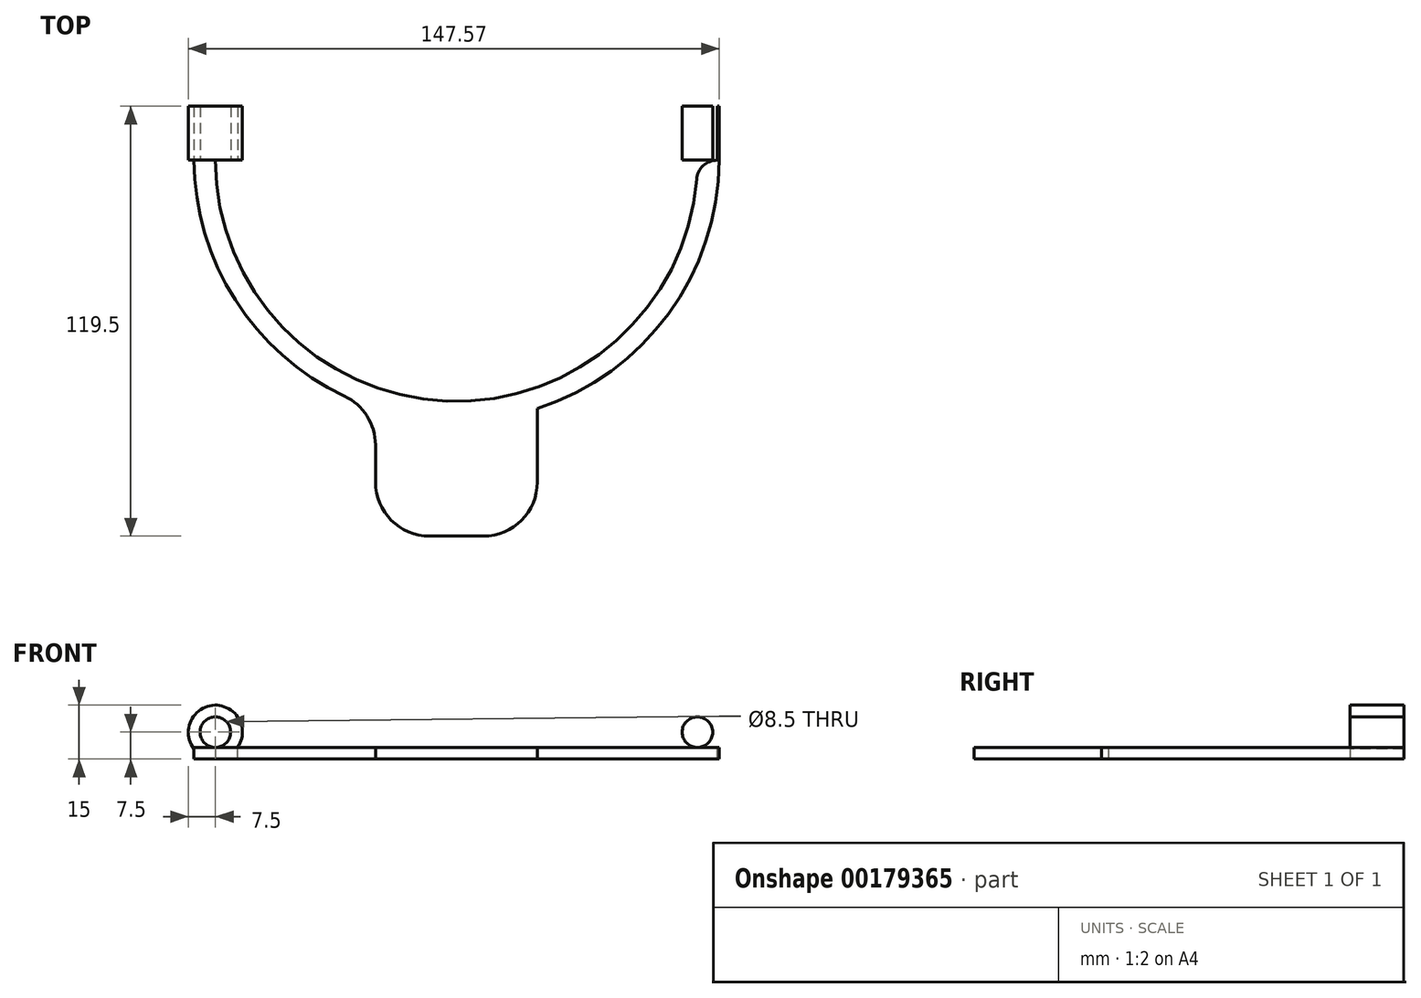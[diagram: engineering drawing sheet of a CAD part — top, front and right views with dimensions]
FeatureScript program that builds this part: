
annotation { "Feature Type Name" : "Feature", "Feature Type Description" : "" }
export const myFeature = defineFeature(function(context is Context, id is Id, definition is map)
    precondition{}
    {
        {
            var Q0;
            Q0=qCreatedBy(makeId("Front.planeOp"),FACE);
            var sketch = newSketch(context, id + "F0", { "sketchPlane" : qUnion([Q0])});
            skLineSegment(sketch, "E0.bottom", {"start": v(67, -4.25) * mm, "end": v(-67, -4.25) * mm, "construction": true});
            skLineSegment(sketch, "E0.top", {"start": v(67, 4.25) * mm, "end": v(-67, 4.25) * mm, "construction": true});
            skLineSegment(sketch, "E0.left", {"start": v(67, -4.25) * mm, "end": v(67, 4.25) * mm, "construction": true});
            skLineSegment(sketch, "E0.right", {"start": v(-67, -4.25) * mm, "end": v(-67, 4.25) * mm, "construction": true});
            skPoint(sketch, "E0.middle", {"position": v(0, 0) * mm});
            skArc(sketch, "E1", {"start": v(67, 4.25) * mm, "mid": v(71.25, 0) * mm, "end": v(67, -4.25) * mm});
            skArc(sketch, "E2", {"start": v(-67, 4.25) * mm, "mid": v(-71.25, 0) * mm, "end": v(-67, -4.25) * mm});
            skArc(sketch, "E3", {"start": v(-67, 4.25) * mm, "mid": v(-62.75, 0) * mm, "end": v(-67, -4.25) * mm});
            skArc(sketch, "E4", {"start": v(67, 4.25) * mm, "mid": v(62.75, 0) * mm, "end": v(67, -4.25) * mm});
            skCircle(sketch, "E5", {"center": v(-67, 0) * mm, "radius": 7.5 * mm});
            skCircle(sketch, "E6", {"center": v(67, 0) * mm, "radius": 7.5 * mm});
            skLineSegment(sketch, "E7.bottom", {"start": v(-67, -4.25) * mm, "end": v(67, -4.25) * mm});
            skLineSegment(sketch, "E7.top", {"start": v(-67, -7.5) * mm, "end": v(67, -7.5) * mm});
            skLineSegment(sketch, "E7.left", {"start": v(-67, -4.25) * mm, "end": v(-67, -7.5) * mm});
            skLineSegment(sketch, "E7.right", {"start": v(67, -4.25) * mm, "end": v(67, -7.5) * mm});
            skSolve(sketch);
        }
        {
            var Q0;
            {var subQ3=sQuery(id+"F0.wireOp",EDGE,"E2");Q0=makeQuery(id+"F0.imprint","IMPRINT",FACE,{"disambiguationData":[TD([[makeQuery(id+"F0.imprint","IMPRINT",EDGE,{"derivedFrom":subQ3}),-1.0]])]});}
            var Q1;
            {var subQ3=sQuery(id+"F0.wireOp",EDGE,"E7.left");Q1=makeQuery(id+"F0.imprint","IMPRINT",FACE,{"disambiguationData":[TD([[makeQuery(id+"F0.imprint","IMPRINT",EDGE,{"derivedFrom":subQ3}),1.0]])]});}
            var Q2;
            {var subQ3=sQuery(id+"F0.wireOp",EDGE,"E7.top");Q2=makeQuery(id+"F0.imprint","IMPRINT",FACE,{"disambiguationData":[TD([[makeQuery(id+"F0.imprint","IMPRINT",EDGE,{"derivedFrom":subQ3}),1.0]])]});}
            var Q3;
            {var subQ0=sQuery(id+"F0.wireOp",EDGE,"E7.right");Q3=makeQuery(id+"F0.imprint","IMPRINT",FACE,{"disambiguationData":[TD([[makeQuery(id+"F0.imprint","IMPRINT",EDGE,{"derivedFrom":subQ0}),-1.0]])]});}
            var Q4;
            {var subQ3=sQuery(id+"F0.wireOp",EDGE,"E1");Q4=makeQuery(id+"F0.imprint","IMPRINT",FACE,{"disambiguationData":[TD([[makeQuery(id+"F0.imprint","IMPRINT",EDGE,{"derivedFrom":subQ3}),1.0]])]});}
            extrude(context, id + "F1", {"entities" : qUnion([Q0, Q1, Q2, Q3, Q4]), "oppositeDirection" : true, "depth" : 15 * mm, "offsetDistance" : 25 * mm});
        }
        {
            var Q0;
            {var subQ3=sQuery(id+"F0.wireOp",EDGE,"E7.top");Q0=makeQuery(id+"F0.imprint","IMPRINT",FACE,{"disambiguationData":[TD([[makeQuery(id+"F0.imprint","IMPRINT",EDGE,{"derivedFrom":subQ3}),1.0]])]});}
            var Q1;
            {var subQ3=sQuery(id+"F0.wireOp",EDGE,"E7.left");Q1=makeQuery(id+"F0.imprint","IMPRINT",FACE,{"disambiguationData":[TD([[makeQuery(id+"F0.imprint","IMPRINT",EDGE,{"derivedFrom":subQ3}),1.0]])]});}
            var Q2;
            {var subQ0=sQuery(id+"F0.wireOp",EDGE,"E7.right");Q2=makeQuery(id+"F0.imprint","IMPRINT",FACE,{"disambiguationData":[TD([[makeQuery(id+"F0.imprint","IMPRINT",EDGE,{"derivedFrom":subQ0}),-1.0]])]});}
            extrude(context, id + "F2", {"entities" : qUnion([Q0, Q1, Q2]), "operationType" : NewBodyOperationType.ADD, "depth" : 50 * mm, "offsetDistance" : 25 * mm});
        }
        {
            var Q0;
            {var subQ0=sQuery(id+"F0.wireOp",EDGE,"E7.bottom");Q0=makeQuery(id+"F2.boolean.opBoolean","MERGE",FACE,{"derivedFrom":[makeQuery(id+"F1.opExtrude","SWEPT_FACE",FACE,{"disambiguationData":[OSD([subQ0])]}),makeQuery(id+"F2.opExtrude","SWEPT_FACE",FACE,{"disambiguationData":[OSD([subQ0])]})]});}
            var sketch = newSketch(context, id + "F3", { "sketchPlane" : qUnion([Q0])});
            skLineSegment(sketch, "E8.bottom", {"start": v(-53.32, 15) * mm, "end": v(53.32, 15) * mm, "construction": true});
            skLineSegment(sketch, "E8.top", {"start": v(-53.32, -15) * mm, "end": v(53.32, -15) * mm, "construction": true});
            skLineSegment(sketch, "E8.left", {"start": v(-53.32, 15) * mm, "end": v(-53.32, -15) * mm, "construction": true});
            skLineSegment(sketch, "E8.right", {"start": v(53.32, 15) * mm, "end": v(53.32, -15) * mm, "construction": true});
            skPoint(sketch, "E8.middle", {"position": v(0, 0) * mm});
            skLineSegment(sketch, "E9", {"start": v(0, 15) * mm, "end": v(0, -50) * mm, "construction": true});
            skArc(sketch, "E10", {"start": v(-67, 0) * mm, "mid": v(0, -67) * mm, "end": v(67, 0) * mm});
            skLineSegment(sketch, "E11", {"start": v(-67, 0) * mm, "end": v(-72.93, 0) * mm, "construction": true});
            skLineSegment(sketch, "E12", {"start": v(67, 0) * mm, "end": v(73.07, 0) * mm, "construction": true});
            skArc(sketch, "E13", {"start": v(-72.93, 0) * mm, "mid": v(0.07, -72.58) * mm, "end": v(73.07, 0) * mm});
            skLineSegment(sketch, "E14", {"start": v(-72.93, 0) * mm, "end": v(-67, 0) * mm});
            skLineSegment(sketch, "E15", {"start": v(67, 0) * mm, "end": v(73.07, 0) * mm});
            skSolve(sketch);
        }
        {
            var Q0;
            {var subQ0=sQuery(id+"F0.wireOp",EDGE,"E7.bottom");Q0=makeQuery(id+"F3.imprint","IMPRINT",FACE,{"disambiguationData":[TD([[makeQuery(id+"F3.imprint","IMPRINT",EDGE,{"derivedFrom":makeQuery(id+"F1.opExtrude","CAP_EDGE",EDGE,{"disambiguationData":[OSD([subQ0])],"isStart":false})}),-1.0]])]});}
            var Q1;
            {var subQ0=sQuery(id+"F3.wireOp",EDGE,"E13");var subQ1=sQuery(id+"F0.wireOp",EDGE,"E7.bottom");var subQ4=makeQuery(id+"F2.opExtrude","CAP_EDGE",EDGE,{"disambiguationData":[OSD([subQ1])],"isStart":false});var subQ5=makeQuery(id+"F3.imprint","INTERSECT",VERTEX,{"disambiguationData":[OD(1.0)],"derivedFrom":[subQ4,subQ0]});Q1=makeQuery(id+"F3.imprint","IMPRINT",FACE,{"disambiguationData":[TD([[makeQuery(id+"F3.imprint","IMPRINT",EDGE,{"disambiguationData":[TD([[subQ5,-1.0]])],"derivedFrom":subQ0}),-1.0]])]});}
            var Q2;
            {var subQ0=sQuery(id+"F3.wireOp",EDGE,"E13");var subQ1=sQuery(id+"F0.wireOp",EDGE,"E7.bottom");var subQ4=makeQuery(id+"F2.opExtrude","CAP_EDGE",EDGE,{"disambiguationData":[OSD([subQ1])],"isStart":false});var subQ5=makeQuery(id+"F3.imprint","INTERSECT",VERTEX,{"disambiguationData":[OD(0.0)],"derivedFrom":[subQ4,subQ0]});Q2=makeQuery(id+"F3.imprint","IMPRINT",FACE,{"disambiguationData":[TD([[makeQuery(id+"F3.imprint","IMPRINT",EDGE,{"disambiguationData":[TD([[subQ5,1.0]])],"derivedFrom":subQ0}),-1.0]])]});}
            extrude(context, id + "F4", {"entities" : qUnion([Q0, Q1, Q2]), "operationType" : NewBodyOperationType.REMOVE, "oppositeDirection" : true, "depth" : 25 * mm, "offsetDistance" : 25 * mm});
        }
        {
            var Q0;
            {var subQ0=sQuery(id+"F3.wireOp",EDGE,"E14");Q0=makeQuery(id+"F3.imprint","IMPRINT",FACE,{"disambiguationData":[TD([[makeQuery(id+"F3.imprint","IMPRINT",EDGE,{"derivedFrom":subQ0}),-1.0]])]});}
            var Q1;
            {var subQ0=sQuery(id+"F3.wireOp",EDGE,"E10");var subQ1=makeQuery(id+"F2.opExtrude","CAP_EDGE",EDGE,{"disambiguationData":[OSD([sQuery(id+"F0.wireOp",EDGE,"E7.bottom")])],"isStart":false});var subQ2=makeQuery(id+"F3.imprint","INTERSECT",VERTEX,{"disambiguationData":[OD(0.0)],"derivedFrom":[subQ1,subQ0]});Q1=makeQuery(id+"F3.imprint","IMPRINT",FACE,{"disambiguationData":[TD([[makeQuery(id+"F3.imprint","IMPRINT",EDGE,{"disambiguationData":[TD([[subQ2,-1.0]])],"derivedFrom":subQ0}),-1.0]])]});}
            var Q2;
            {var subQ0=sQuery(id+"F3.wireOp",EDGE,"E15");Q2=makeQuery(id+"F3.imprint","IMPRINT",FACE,{"disambiguationData":[TD([[makeQuery(id+"F3.imprint","IMPRINT",EDGE,{"derivedFrom":subQ0}),-1.0]])]});}
            var Q3;
            {var subQ0=sQuery(id+"F0.wireOp",EDGE,"E7.left");var subQ1=sQuery(id+"F0.wireOp",EDGE,"E7.top");var subQ3=makeQuery(id+"F2.opExtrude","SWEPT_FACE",FACE,{"disambiguationData":[OSD([subQ0])]});Q3=makeQuery(id+"F4.boolean.opBoolean","SPLIT",FACE,{"disambiguationData":[TD([subQ3])],"derivedFrom":makeQuery(id+"F2.boolean.opBoolean","MERGE",FACE,{"derivedFrom":[makeQuery(id+"F1.opExtrude","SWEPT_FACE",FACE,{"disambiguationData":[OSD([subQ1])]}),makeQuery(id+"F2.opExtrude","SWEPT_FACE",FACE,{"disambiguationData":[OSD([subQ1])]})]})});}
            extrude(context, id + "F5", {"entities" : qUnion([Q0, Q1, Q2]), "operationType" : NewBodyOperationType.ADD, "endBound" : BoundingType.UP_TO_SURFACE, "oppositeDirection" : true, "depth" : 25 * mm, "endBoundEntityFace" : qUnion([Q3]), "offsetDistance" : 25 * mm});
        }
        {
            var Q0;
            {var subQ0=sQuery(id+"F3.wireOp",EDGE,"E14");var subQ1=sQuery(id+"F3.wireOp",EDGE,"E10");var subQ2=sQuery(id+"F0.wireOp",EDGE,"E7.left");var subQ3=sQuery(id+"F0.wireOp",EDGE,"E7.bottom");var subQ4=sQuery(id+"F0.wireOp",EDGE,"E3");var subQ5=sQuery(id+"F0.wireOp",EDGE,"E2");Q0=makeQuery(id+"F5.boolean.opBoolean","MERGE",EDGE,{"derivedFrom":[makeQuery(id+"F4.boolean.opBoolean","MERGE",EDGE,{"derivedFrom":[makeQuery(id+"F2.opExtrude","CAP_EDGE",EDGE,{"disambiguationData":[OSD([subQ2])],"isStart":true})],"fromTools":[makeQuery(id+"F4.opExtrude","SWEPT_EDGE",EDGE,{"disambiguationData":[OSD([subQ5,subQ4,subQ3,subQ2,subQ1,subQ0])]})]}),makeQuery(id+"F5.opExtrude","SWEPT_EDGE",EDGE,{"disambiguationData":[OSD([subQ5,subQ4,subQ3,subQ2,subQ1,subQ0])]})]});}
            var Q1;
            {var subQ0=sQuery(id+"F3.wireOp",EDGE,"E15");var subQ1=sQuery(id+"F3.wireOp",EDGE,"E10");var subQ2=sQuery(id+"F0.wireOp",EDGE,"E7.right");var subQ3=sQuery(id+"F0.wireOp",EDGE,"E7.bottom");var subQ4=sQuery(id+"F0.wireOp",EDGE,"E4");var subQ5=sQuery(id+"F0.wireOp",EDGE,"E1");Q1=makeQuery(id+"F5.boolean.opBoolean","MERGE",EDGE,{"derivedFrom":[makeQuery(id+"F4.boolean.opBoolean","MERGE",EDGE,{"derivedFrom":[makeQuery(id+"F2.opExtrude","CAP_EDGE",EDGE,{"disambiguationData":[OSD([subQ2])],"isStart":true})],"fromTools":[makeQuery(id+"F4.opExtrude","SWEPT_EDGE",EDGE,{"disambiguationData":[OSD([subQ5,subQ4,subQ3,subQ2,subQ1,subQ0])]})]}),makeQuery(id+"F5.opExtrude","SWEPT_EDGE",EDGE,{"disambiguationData":[OSD([subQ5,subQ4,subQ3,subQ2,subQ1,subQ0])]})]});}
            fillet(context, id + "F6", {"entities" : qUnion([Q0, Q1]), "tangentPropagation" : true, "radius" : 5.75 * mm, "defaultsChanged" : false, "vertexSettings" : [], "allowEdgeOverflow" : false});
        }
        {
            var Q0;
            Q0=makeQuery(id+"F5.opExtrude","SWEPT_FACE",FACE,{"disambiguationData":[OSD([sQuery(id+"F3.wireOp",EDGE,"E14")])]});
            var Q1;
            Q1=makeQuery(id+"F5.opExtrude","SWEPT_FACE",FACE,{"disambiguationData":[OSD([sQuery(id+"F3.wireOp",EDGE,"E15")])]});
            var Q2;
            {var subQ0=sQuery(id+"F0.wireOp",EDGE,"E7.top");var subQ1=sQuery(id+"F0.wireOp",EDGE,"E6");var subQ2=sQuery(id+"F0.wireOp",EDGE,"E4");var subQ3=sQuery(id+"F0.wireOp",EDGE,"E1");var subQ4=sQuery(id+"F0.wireOp",EDGE,"E7.bottom");Q2=makeQuery(id+"F4.boolean.opBoolean","SPLIT",FACE,{"disambiguationData":[TD([makeQuery(id+"F1.opExtrude","SWEPT_FACE",FACE,{"disambiguationData":[OSD([subQ1])]})])],"derivedFrom":makeQuery(id+"F1.opExtrude","CAP_FACE",FACE,{"disambiguationData":[OSD([subQ3,sQuery(id+"F0.wireOp",EDGE,"E2"),sQuery(id+"F0.wireOp",EDGE,"E3"),subQ2,sQuery(id+"F0.wireOp",EDGE,"E5"),subQ1,subQ4,subQ0])],"isStart":false})});}
            extrude(context, id + "F7", {"entities" : qUnion([Q0, Q1]), "operationType" : NewBodyOperationType.ADD, "endBound" : BoundingType.UP_TO_SURFACE, "depth" : 25 * mm, "endBoundEntityFace" : qUnion([Q2]), "offsetDistance" : 25 * mm});
        }
        {
            var Q0;
            {var subQ0=sQuery(id+"F3.wireOp",EDGE,"E10");var subQ1=makeQuery(id+"F2.opExtrude","CAP_EDGE",EDGE,{"disambiguationData":[OSD([sQuery(id+"F0.wireOp",EDGE,"E7.bottom")])],"isStart":false});var subQ2=makeQuery(id+"F3.imprint","INTERSECT",VERTEX,{"disambiguationData":[OD(0.0)],"derivedFrom":[subQ1,subQ0]});Q0=makeQuery(id+"F3.imprint","IMPRINT",FACE,{"disambiguationData":[TD([[makeQuery(id+"F3.imprint","IMPRINT",EDGE,{"disambiguationData":[TD([[subQ2,-1.0]])],"derivedFrom":subQ0}),-1.0]])]});}
            var sketch = newSketch(context, id + "F8", { "sketchPlane" : qUnion([Q0])});
            skLineSegment(sketch, "E16.bottom", {"start": v(22.5, -104.5) * mm, "end": v(-22.5, -104.5) * mm});
            skLineSegment(sketch, "E16.top", {"start": v(22.5, -29.5) * mm, "end": v(-22.5, -29.5) * mm});
            skLineSegment(sketch, "E16.left", {"start": v(22.5, -104.5) * mm, "end": v(22.5, -29.5) * mm});
            skLineSegment(sketch, "E16.right", {"start": v(-22.5, -104.5) * mm, "end": v(-22.5, -29.5) * mm});
            skPoint(sketch, "E16.middle", {"position": v(0, -67) * mm});
            skLineSegment(sketch, "E17", {"start": v(0, -67) * mm, "end": v(0, 0) * mm, "construction": true});
            skSolve(sketch);
        }
        {
            var Q0;
            {var subQ0=sQuery(id+"F8.wireOp",EDGE,"E16.bottom");Q0=makeQuery(id+"F8.imprint","IMPRINT",FACE,{"disambiguationData":[TD([[makeQuery(id+"F8.imprint","IMPRINT",EDGE,{"derivedFrom":subQ0}),-1.0]])]});}
            var Q1;
            {var subQ0=sQuery(id+"F3.wireOp",EDGE,"E15");var subQ1=sQuery(id+"F3.wireOp",EDGE,"E14");var subQ2=sQuery(id+"F3.wireOp",EDGE,"E13");var subQ3=sQuery(id+"F0.wireOp",EDGE,"E7.right");var subQ4=sQuery(id+"F0.wireOp",EDGE,"E7.bottom");var subQ5=sQuery(id+"F0.wireOp",EDGE,"E4");var subQ6=sQuery(id+"F0.wireOp",EDGE,"E1");var subQ7=sQuery(id+"F0.wireOp",EDGE,"E7.left");var subQ8=sQuery(id+"F0.wireOp",EDGE,"E3");var subQ9=sQuery(id+"F0.wireOp",EDGE,"E2");var subQ10=sQuery(id+"F3.wireOp",EDGE,"E10");var subQ11=sQuery(id+"F0.wireOp",EDGE,"E7.top");var subQ14=sQuery(id+"F0.wireOp",EDGE,"E6");var subQ15=makeQuery(id+"F1.opExtrude","SWEPT_FACE",FACE,{"disambiguationData":[OSD([subQ14])]});var subQ16=sQuery(id+"F0.wireOp",EDGE,"E5");var subQ19=makeQuery(id+"F2.opExtrude","SWEPT_FACE",FACE,{"disambiguationData":[OSD([subQ3])]});var subQ24=makeQuery(id+"F2.boolean.opBoolean","MERGE",FACE,{"derivedFrom":[makeQuery(id+"F1.opExtrude","SWEPT_FACE",FACE,{"disambiguationData":[OSD([subQ11])]}),makeQuery(id+"F2.opExtrude","SWEPT_FACE",FACE,{"disambiguationData":[OSD([subQ11])]})]});var subQ25=makeQuery(id+"F2.opExtrude","SWEPT_FACE",FACE,{"disambiguationData":[OSD([subQ7])]});var subQ26=makeQuery(id+"F1.opExtrude","SWEPT_FACE",FACE,{"disambiguationData":[OSD([subQ16])]});Q1=makeQuery(id+"F7.boolean.opBoolean","MERGE",FACE,{"derivedFrom":[makeQuery(id+"F6.opFillet","MERGE",FACE,{"derivedFrom":[makeQuery(id+"F4.boolean.opBoolean","SPLIT",FACE,{"disambiguationData":[TD([subQ26])],"derivedFrom":subQ24}),makeQuery(id+"F4.boolean.opBoolean","SPLIT",FACE,{"disambiguationData":[TD([subQ15])],"derivedFrom":subQ24}),makeQuery(id+"F5.boolean.opBoolean","MERGE",FACE,{"derivedFrom":[makeQuery(id+"F4.boolean.opBoolean","SPLIT",FACE,{"disambiguationData":[TD([subQ25])],"derivedFrom":subQ24}),makeQuery(id+"F4.boolean.opBoolean","SPLIT",FACE,{"disambiguationData":[TD([subQ19])],"derivedFrom":subQ24}),makeQuery(id+"F5.opExtrude","CAP_FACE",FACE,{"disambiguationData":[OSD([subQ4,subQ10,subQ2])],"isStart":false}),makeQuery(id+"F5.opExtrude","CAP_FACE",FACE,{"disambiguationData":[OSD([subQ9,subQ8,subQ4,subQ7,subQ2,subQ1])],"isStart":false}),makeQuery(id+"F5.opExtrude","CAP_FACE",FACE,{"disambiguationData":[OSD([subQ6,subQ5,subQ4,subQ3,subQ2,subQ0])],"isStart":false})]})]}),makeQuery(id+"F7.opExtrude","SWEPT_FACE",FACE,{"disambiguationData":[OSD([subQ1])]}),makeQuery(id+"F7.opExtrude","SWEPT_FACE",FACE,{"disambiguationData":[OSD([subQ0])]})]});}
            extrude(context, id + "F9", {"entities" : qUnion([Q0]), "operationType" : NewBodyOperationType.ADD, "endBound" : BoundingType.UP_TO_SURFACE, "oppositeDirection" : true, "depth" : 25 * mm, "endBoundEntityFace" : qUnion([Q1]), "offsetDistance" : 25 * mm});
        }
        {
            var Q0;
            Q0=makeQuery(id+"F9.opExtrude","SWEPT_EDGE",EDGE,{"disambiguationData":[OSD([sQuery(id+"F3.wireOp",EDGE,"E13"),sQuery(id+"F8.wireOp",EDGE,"E16.left")])]});
            var Q1;
            Q1=makeQuery(id+"F9.opExtrude","SWEPT_EDGE",EDGE,{"disambiguationData":[OSD([sQuery(id+"F3.wireOp",EDGE,"E13"),sQuery(id+"F8.wireOp",EDGE,"E16.right")])]});
            var Q2;
            Q2=makeQuery(id+"F9.opExtrude","SWEPT_EDGE",EDGE,{"disambiguationData":[OSD([sQuery(id+"F8.wireOp",EDGE,"E16.bottom"),sQuery(id+"F8.wireOp",EDGE,"E16.right")])]});
            var Q3;
            Q3=makeQuery(id+"F9.opExtrude","SWEPT_EDGE",EDGE,{"disambiguationData":[OSD([sQuery(id+"F8.wireOp",EDGE,"E16.bottom"),sQuery(id+"F8.wireOp",EDGE,"E16.left")])]});
            fillet(context, id + "F10", {"entities" : qUnion([Q0, Q1, Q2, Q3]), "tangentPropagation" : true, "radius" : 15 * mm, "defaultsChanged" : true, "vertexSettings" : [], "allowEdgeOverflow" : false});
        }
    });
